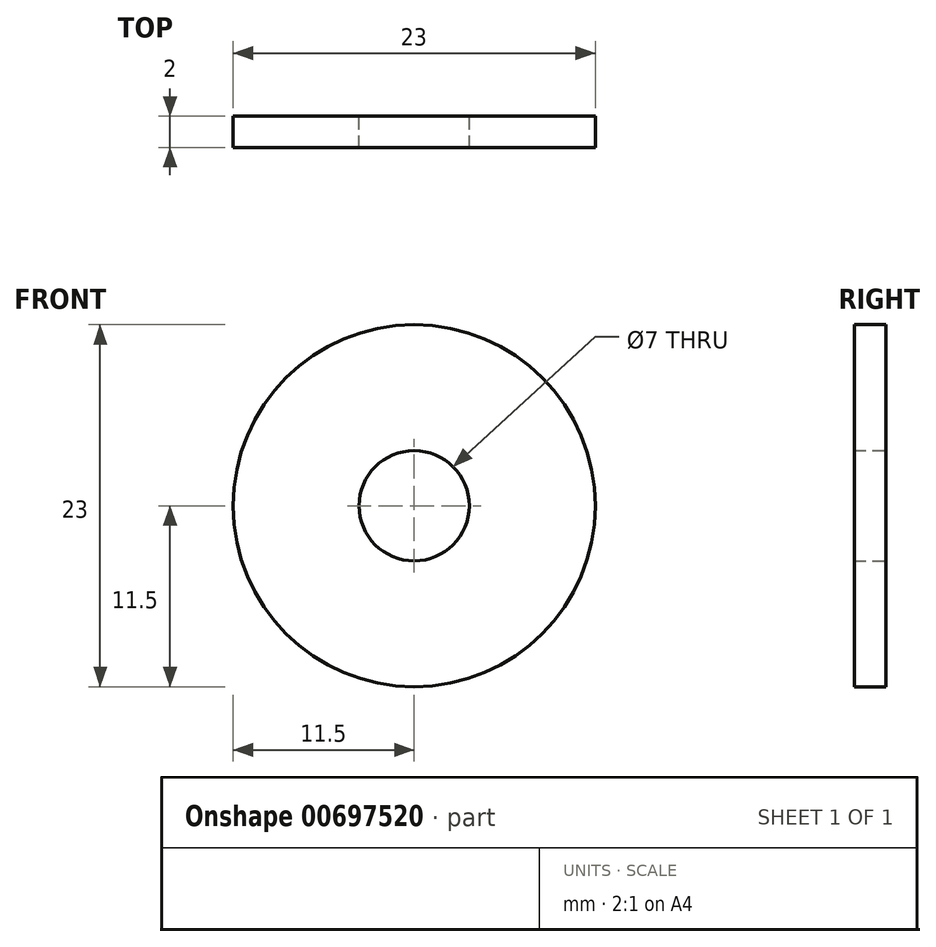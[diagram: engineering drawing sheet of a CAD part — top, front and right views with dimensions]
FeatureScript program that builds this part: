
annotation { "Feature Type Name" : "Feature", "Feature Type Description" : "" }
export const myFeature = defineFeature(function(context is Context, id is Id, definition is map)
    precondition{}
    {
        {
            var Q0;
            Q0=qCreatedBy(makeId("Front.planeOp"),FACE);
            var sketch = newSketch(context, id + "F0", { "sketchPlane" : qUnion([Q0])});
            skCircle(sketch, "E0", {"center": v(0, 0) * mm, "radius": 11.5 * mm});
            skCircle(sketch, "E1", {"center": v(0, 0) * mm, "radius": 3.5 * mm});
            skSolve(sketch);
        }
        {
            var Q0;
            Q0=makeQuery(id+"F0.imprint","IMPRINT",FACE,{"disambiguationData":[TD([[makeQuery(id+"F0.imprint","IMPRINT",EDGE,{"derivedFrom":sQuery(id+"F0.wireOp",EDGE,"E0")}),1.0]])]});
            extrude(context, id + "F1", {"entities" : qUnion([Q0]), "depth" : 2 * mm, "offsetDistance" : 25 * mm});
        }
    });
